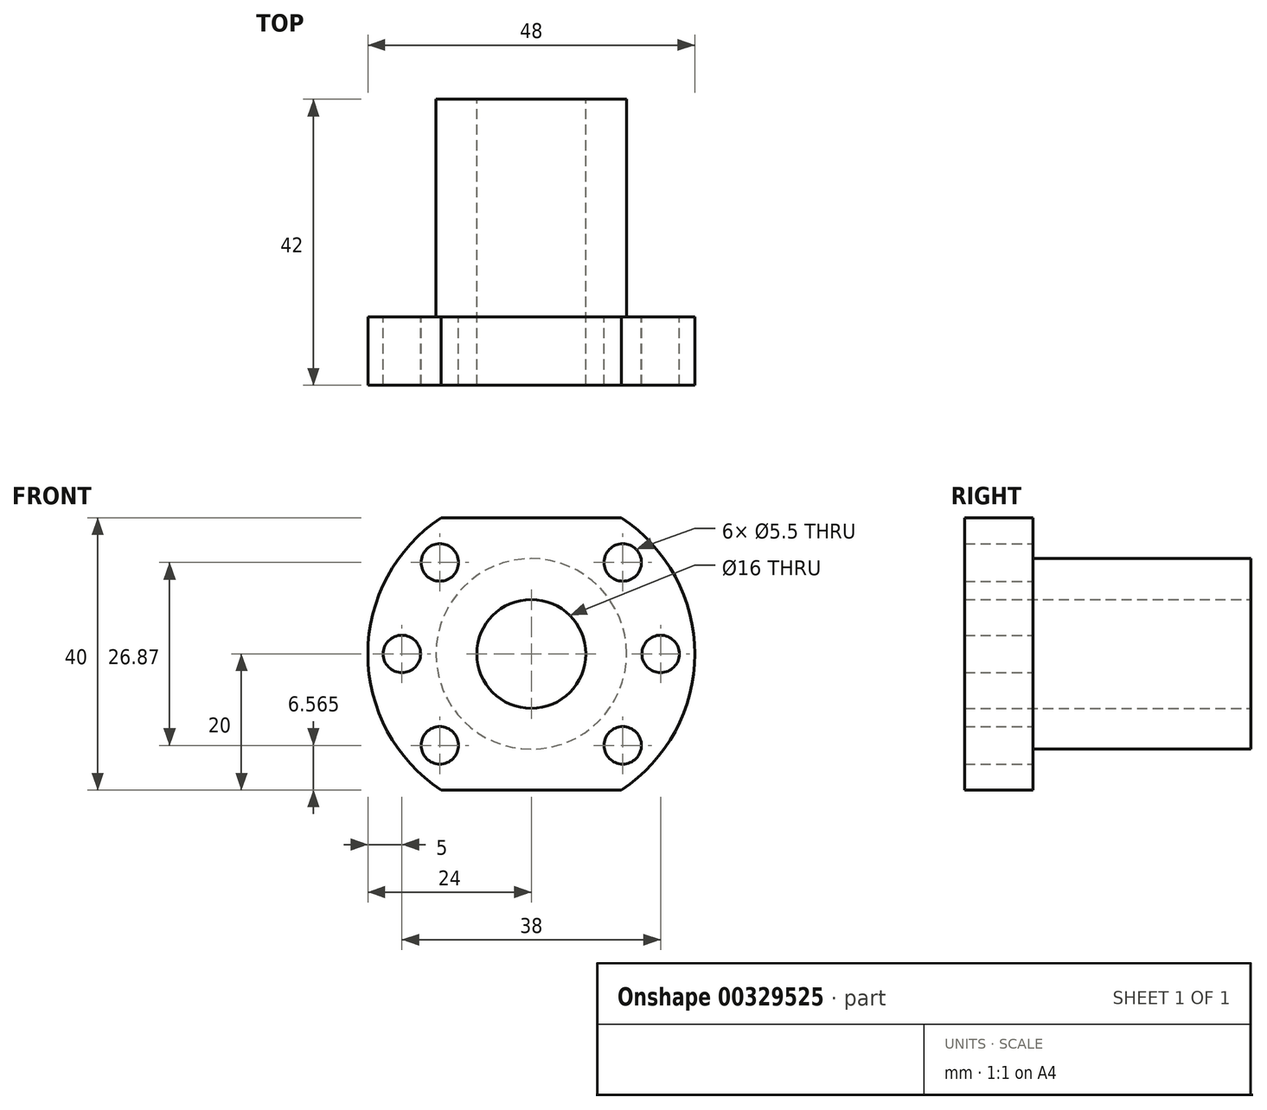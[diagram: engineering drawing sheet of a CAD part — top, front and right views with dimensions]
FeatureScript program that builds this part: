
annotation { "Feature Type Name" : "Feature", "Feature Type Description" : "" }
export const myFeature = defineFeature(function(context is Context, id is Id, definition is map)
    precondition{}
    {
        {
            var Q0;
            Q0=qCreatedBy(makeId("Front.planeOp"),FACE);
            var sketch = newSketch(context, id + "F0", { "sketchPlane" : qUnion([Q0])});
            skArc(sketch, "E0", {"start": v(-13.27, 20) * mm, "mid": v(-24, 0) * mm, "end": v(-13.27, -20) * mm});
            skCircle(sketch, "E1", {"center": v(0, 0) * mm, "radius": 8 * mm});
            skLineSegment(sketch, "E2", {"start": v(-13.27, 20) * mm, "end": v(13.27, 20) * mm});
            skLineSegment(sketch, "E3", {"start": v(-13.27, -20) * mm, "end": v(13.27, -20) * mm});
            skArc(sketch, "E4.trimOffspring", {"start": v(13.27, -20) * mm, "mid": v(24, 0) * mm, "end": v(13.27, 20) * mm});
            skCircle(sketch, "E5", {"center": v(0, 0) * mm, "radius": 19 * mm, "construction": true});
            skCircle(sketch, "E6", {"center": v(-13.44, 13.44) * mm, "radius": 2.75 * mm});
            skCircle(sketch, "E7", {"center": v(-19, 0) * mm, "radius": 2.75 * mm});
            skCircle(sketch, "E8", {"center": v(-13.44, -13.44) * mm, "radius": 2.75 * mm});
            skCircle(sketch, "E9", {"center": v(13.44, -13.44) * mm, "radius": 2.75 * mm});
            skCircle(sketch, "E10", {"center": v(19, 0) * mm, "radius": 2.75 * mm});
            skCircle(sketch, "E11", {"center": v(13.44, 13.44) * mm, "radius": 2.75 * mm});
            skLineSegment(sketch, "E12", {"start": v(-13.44, 13.44) * mm, "end": v(0, 0) * mm, "construction": true});
            skLineSegment(sketch, "E13", {"start": v(-19, 0) * mm, "end": v(0, 0) * mm, "construction": true});
            skSolve(sketch);
        }
        {
            var Q0;
            Q0 = qSketchRegion(id + "F0", true);
            extrude(context, id + "F1", {"entities" : qUnion([Q0]), "depth" : 10 * mm});
        }
        {
            var Q0;
            Q0=makeQuery(id+"F1.opExtrude","CAP_FACE",FACE,{"disambiguationData":[OSD([sQuery(id+"F0.wireOp",EDGE,"E0"),sQuery(id+"F0.wireOp",EDGE,"E1"),sQuery(id+"F0.wireOp",EDGE,"E2"),sQuery(id+"F0.wireOp",EDGE,"E3"),sQuery(id+"F0.wireOp",EDGE,"E4.trimOffspring"),sQuery(id+"F0.wireOp",EDGE,"E6"),sQuery(id+"F0.wireOp",EDGE,"E7"),sQuery(id+"F0.wireOp",EDGE,"E8"),sQuery(id+"F0.wireOp",EDGE,"E9"),sQuery(id+"F0.wireOp",EDGE,"E10"),sQuery(id+"F0.wireOp",EDGE,"E11")])],"isStart":true});
            var sketch = newSketch(context, id + "F2", { "sketchPlane" : qUnion([Q0])});
            skCircle(sketch, "E14", {"center": v(0, 0) * mm, "radius": 8 * mm});
            skCircle(sketch, "E15", {"center": v(0, 0) * mm, "radius": 14 * mm});
            skSolve(sketch);
        }
        {
            var Q0;
            Q0 = qSketchRegion(id + "F2", true);
            extrude(context, id + "F3", {"entities" : qUnion([Q0]), "operationType" : NewBodyOperationType.ADD, "depth" : 32 * mm});
        }
    });
